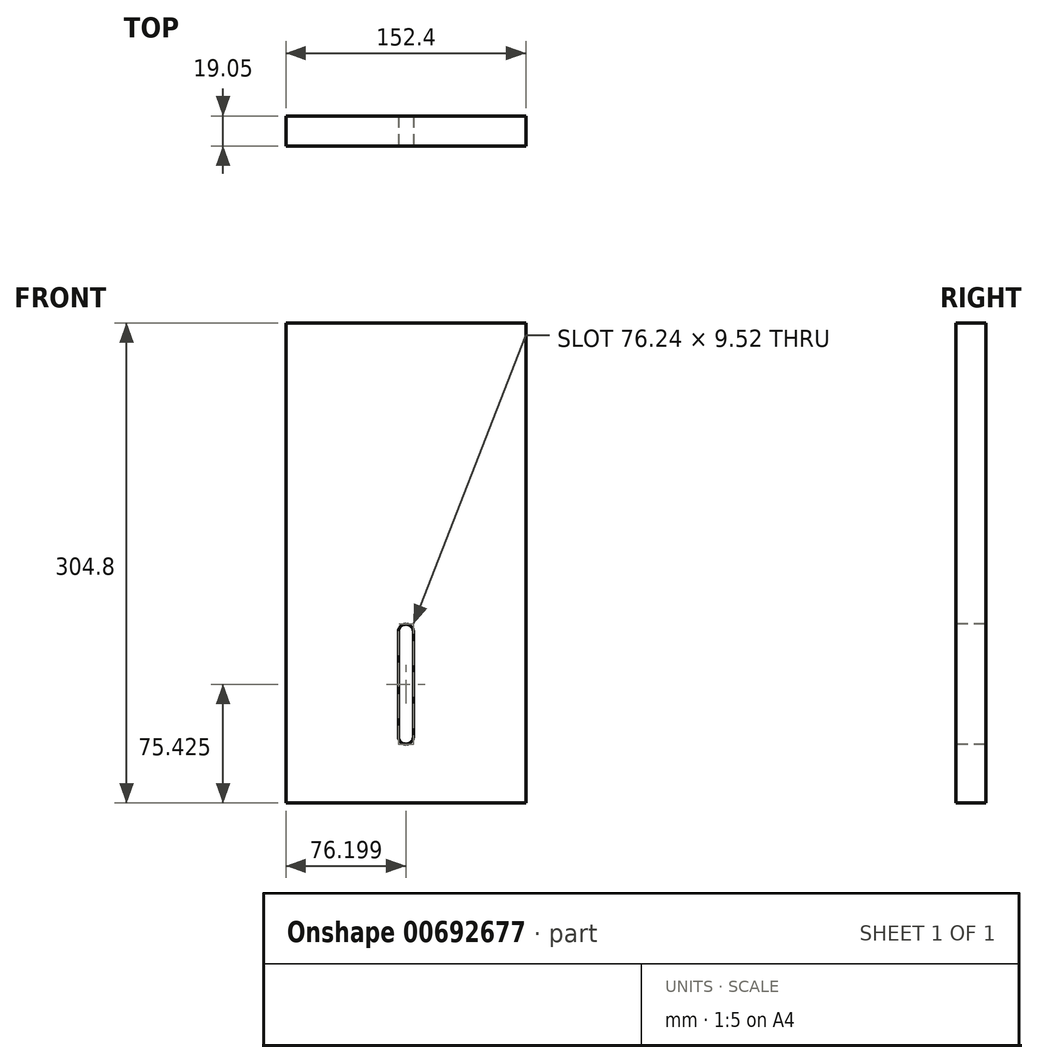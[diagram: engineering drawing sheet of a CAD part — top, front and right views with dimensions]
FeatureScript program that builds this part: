
annotation { "Feature Type Name" : "Feature", "Feature Type Description" : "" }
export const myFeature = defineFeature(function(context is Context, id is Id, definition is map)
    precondition{}
    {
        {
            var Q0;
            Q0=qCreatedBy(makeId("Front.planeOp"),FACE);
            var sketch = newSketch(context, id + "F0", { "sketchPlane" : qUnion([Q0])});
            skLineSegment(sketch, "E0.bottom", {"start": v(-92.66, 141.31) * mm, "end": v(59.74, 141.31) * mm});
            skLineSegment(sketch, "E0.top", {"start": v(-92.66, -163.49) * mm, "end": v(59.74, -163.49) * mm});
            skLineSegment(sketch, "E0.left", {"start": v(-92.66, 141.31) * mm, "end": v(-92.66, -163.49) * mm});
            skLineSegment(sketch, "E0.right", {"start": v(59.74, 141.31) * mm, "end": v(59.74, -163.49) * mm});
            skPoint(sketch, "E1", {"position": v(-16.46, -11.09) * mm});
            skPoint(sketch, "E2", {"position": v(-16.46, -119.04) * mm});
            skSolve(sketch);
        }
        {
            var Q0;
            Q0=makeQuery(id+"F0.imprint","IMPRINT",FACE,{"disambiguationData":[TD([[makeQuery(id+"F0.imprint","IMPRINT",EDGE,{"derivedFrom":sQuery(id+"F0.wireOp",EDGE,"E0.bottom")}),-1.0]])]});
            extrude(context, id + "F1", {"entities" : qUnion([Q0]), "depth" : 19.05 * mm, "offsetDistance" : 25.4 * mm});
        }
        {
            var Q0;
            Q0=makeQuery(id+"F1.opExtrude","CAP_FACE",FACE,{"disambiguationData":[OSD([sQuery(id+"F0.wireOp",EDGE,"E0.bottom"),sQuery(id+"F0.wireOp",EDGE,"E0.top"),sQuery(id+"F0.wireOp",EDGE,"E0.left"),sQuery(id+"F0.wireOp",EDGE,"E0.right")])],"isStart":false});
            var sketch = newSketch(context, id + "F2", { "sketchPlane" : qUnion([Q0])});
            skPoint(sketch, "E3", {"position": v(-16.46, -54.71) * mm});
            skPoint(sketch, "E4", {"position": v(-16.46, -121.42) * mm});
            skLineSegment(sketch, "E5.right", {"start": v(-11.7, -54.71) * mm, "end": v(-11.7, -121.42) * mm});
            skLineSegment(sketch, "E6.right", {"start": v(-21.22, -54.71) * mm, "end": v(-21.22, -121.42) * mm});
            skArc(sketch, "E7", {"start": v(-11.7, -54.71) * mm, "mid": v(-16.46, -49.95) * mm, "end": v(-21.22, -54.71) * mm});
            skArc(sketch, "E8", {"start": v(-21.22, -121.42) * mm, "mid": v(-16.46, -126.18) * mm, "end": v(-11.7, -121.42) * mm});
            skSolve(sketch);
        }
        {
            var Q0;
            Q0=makeQuery(id+"F2.imprint","IMPRINT",FACE,{"disambiguationData":[TD([[makeQuery(id+"F2.imprint","IMPRINT",EDGE,{"derivedFrom":sQuery(id+"F2.wireOp",EDGE,"E5.right")}),-1.0]])]});
            extrude(context, id + "F3", {"entities" : qUnion([Q0]), "operationType" : NewBodyOperationType.REMOVE, "oppositeDirection" : true, "depth" : 19.05 * mm, "offsetDistance" : 25.4 * mm});
        }
    });
